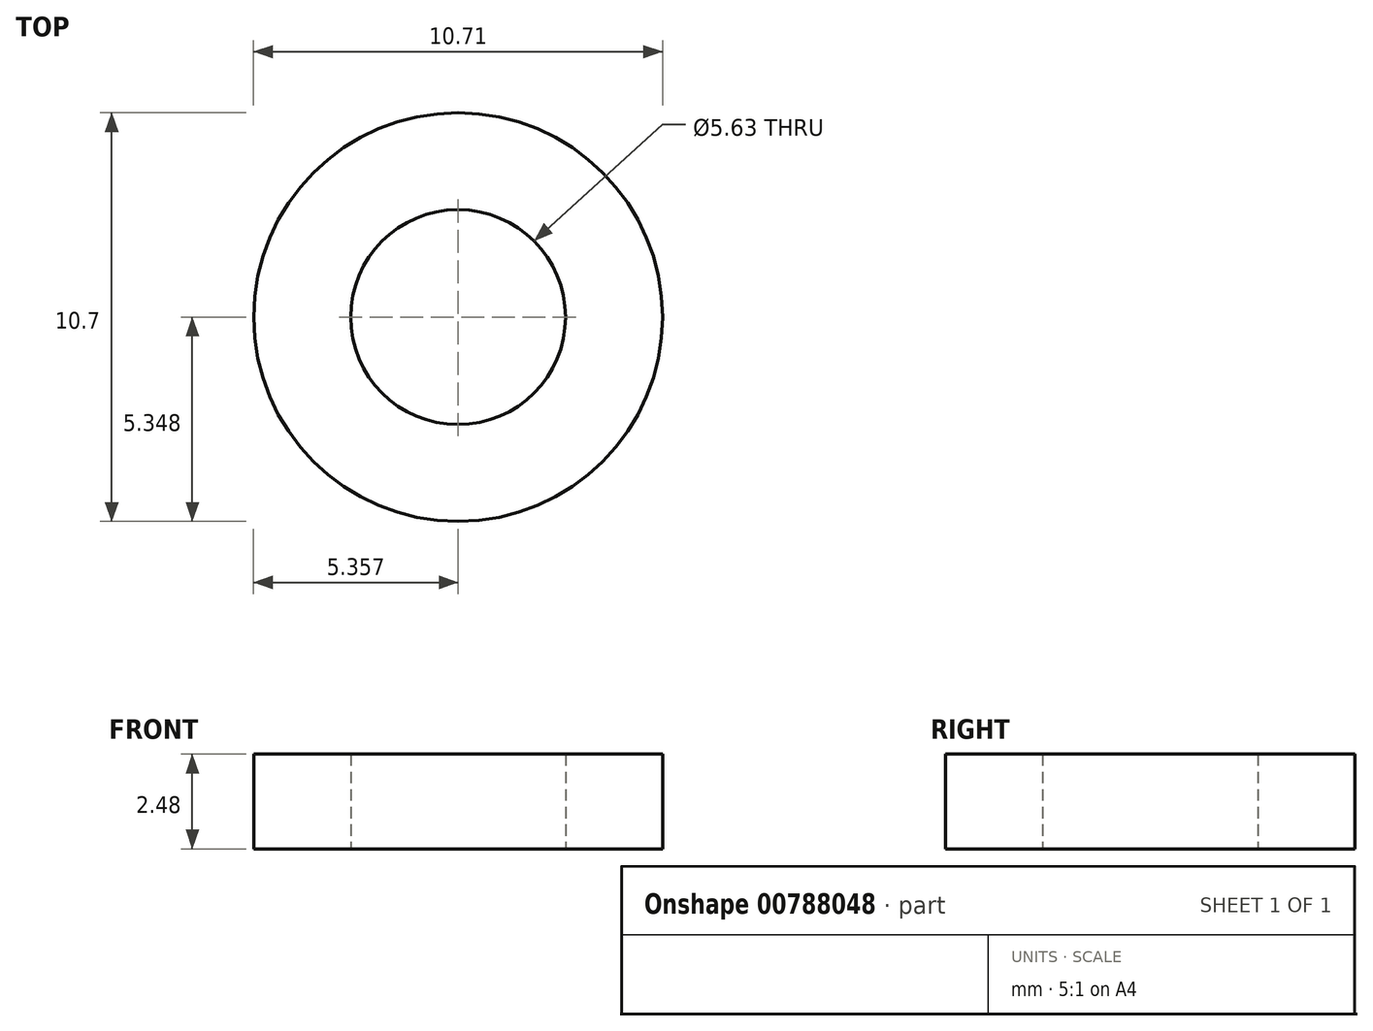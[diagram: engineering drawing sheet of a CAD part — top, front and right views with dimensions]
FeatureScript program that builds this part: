
annotation { "Feature Type Name" : "Feature", "Feature Type Description" : "" }
export const myFeature = defineFeature(function(context is Context, id is Id, definition is map)
    precondition{}
    {
        {
            var Q0;
            Q0=qCreatedBy(makeId("Top.planeOp"),FACE);
            var sketch = newSketch(context, id + "F0", { "sketchPlane" : qUnion([Q0])});
            skCircle(sketch, "E0", {"center": v(-15.2, 16.28) * mm, "radius": 5.35 * mm});
            skCircle(sketch, "E1", {"center": v(-15.2, 16.28) * mm, "radius": 2.81 * mm});
            skSolve(sketch);
        }
        {
            var Q0;
            Q0 = qSketchRegion(id + "F0", true);
            extrude(context, id + "F1", {"entities" : qUnion([Q0]), "depth" : 2.48 * mm, "offsetDistance" : 25 * mm});
        }
    });
